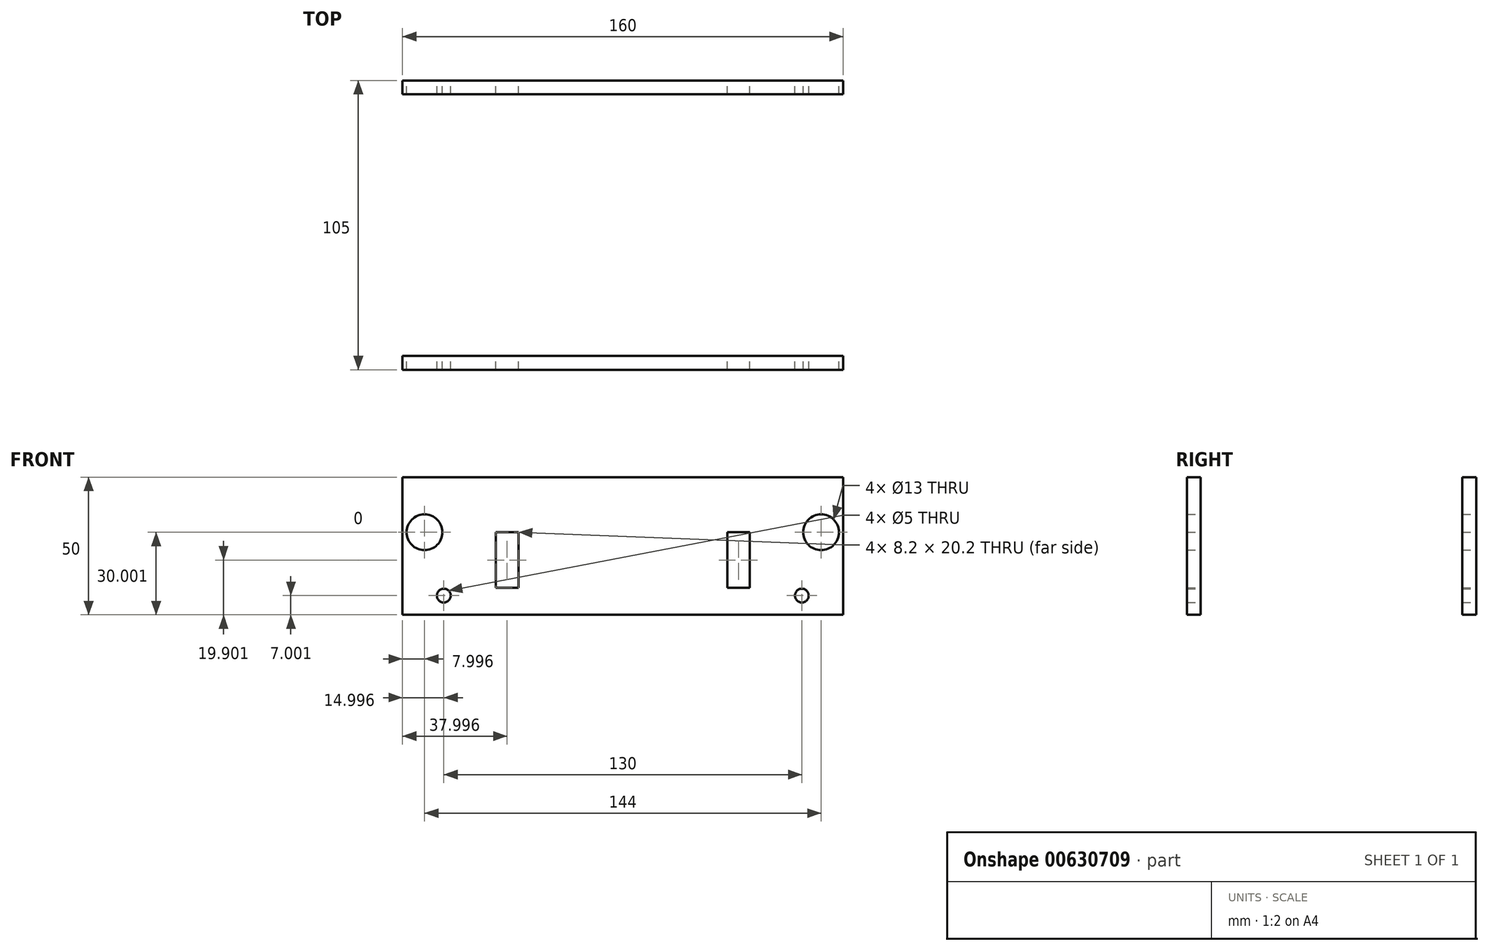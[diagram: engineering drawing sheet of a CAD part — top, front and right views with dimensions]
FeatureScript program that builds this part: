
annotation { "Feature Type Name" : "Feature", "Feature Type Description" : "" }
export const myFeature = defineFeature(function(context is Context, id is Id, definition is map)
    precondition{}
    {
        {
            var Q0;
            Q0=qCreatedBy(makeId("Front.planeOp"),FACE);
            var sketch = newSketch(context, id + "F0", { "sketchPlane" : qUnion([Q0])});
            skLineSegment(sketch, "E0.bottom", {"start": v(-54.53, 15.8) * mm, "end": v(105.47, 15.8) * mm});
            skLineSegment(sketch, "E0.top", {"start": v(-54.53, -34.2) * mm, "end": v(105.47, -34.2) * mm});
            skLineSegment(sketch, "E0.left", {"start": v(-54.53, 15.8) * mm, "end": v(-54.53, -34.2) * mm});
            skLineSegment(sketch, "E0.right", {"start": v(105.47, 15.8) * mm, "end": v(105.47, -34.2) * mm});
            skCircle(sketch, "E1", {"center": v(97.47, -4.2) * mm, "radius": 6.5 * mm});
            skLineSegment(sketch, "E2", {"start": v(25.47, 15.8) * mm, "end": v(25.47, -35.8) * mm, "construction": true});
            skPoint(sketch, "E2.endSnap0", {"position": v(25.47, -34.2) * mm});
            skLineSegment(sketch, "E3.bottom", {"start": v(63.37, -4.2) * mm, "end": v(71.57, -4.2) * mm});
            skLineSegment(sketch, "E3.top", {"start": v(63.37, -24.4) * mm, "end": v(71.57, -24.4) * mm});
            skLineSegment(sketch, "E3.left", {"start": v(63.37, -4.2) * mm, "end": v(63.37, -24.4) * mm});
            skLineSegment(sketch, "E3.right", {"start": v(71.57, -4.2) * mm, "end": v(71.57, -24.4) * mm});
            skLineSegment(sketch, "E4.MirrorCS", {"start": v(-12.43, -4.2) * mm, "end": v(-12.43, -24.4) * mm});
            skLineSegment(sketch, "E5.MirrorCS", {"start": v(-20.63, -4.2) * mm, "end": v(-20.63, -24.4) * mm});
            skLineSegment(sketch, "E6.MirrorCS", {"start": v(-12.43, -4.2) * mm, "end": v(-20.63, -4.2) * mm});
            skLineSegment(sketch, "E7.MirrorCS", {"start": v(-12.43, -24.4) * mm, "end": v(-20.63, -24.4) * mm});
            skCircle(sketch, "E8.MirrorC", {"center": v(-46.53, -4.2) * mm, "radius": 6.5 * mm});
            skPoint(sketch, "E9", {"position": v(67.47, -24.4) * mm});
            skPoint(sketch, "E10", {"position": v(-16.53, -24.4) * mm});
            skCircle(sketch, "E11", {"center": v(90.47, -27.2) * mm, "radius": 2.5 * mm});
            skCircle(sketch, "E12.MirrorC", {"center": v(-39.53, -27.2) * mm, "radius": 2.5 * mm});
            skSolve(sketch);
        }
        {
            var Q0;
            Q0 = qSketchRegion(id + "F0", true);
            extrude(context, id + "F1", {"entities" : qUnion([Q0]), "depth" : 5 * mm, "offsetDistance" : 25 * mm});
        }
        {
            var Q0;
            Q0=makeQuery(id+"F1.opExtrude","SWEPT_BODY",BODY,{"disambiguationData":[OSD([sQuery(id+"F0.wireOp",EDGE,"E0.bottom"),sQuery(id+"F0.wireOp",EDGE,"E0.top"),sQuery(id+"F0.wireOp",EDGE,"E0.left"),sQuery(id+"F0.wireOp",EDGE,"E0.right"),sQuery(id+"F0.wireOp",EDGE,"E1"),sQuery(id+"F0.wireOp",EDGE,"QShWiYwr-2bT6-ZryE-rk6D-aJS2m8MRligL"),sQuery(id+"F0.wireOp",EDGE,"d1fae640-989b-4966-b3a4-efb05116fdd30.MirrorC"),sQuery(id+"F0.wireOp",EDGE,"fb1e3ab4-b454-426e-8810-0b7114d907bb0.MirrorC")])]});
            transform(context, id + "F2", {"entities" : qUnion([Q0]), "transformType" : TransformType.TRANSLATION_3D, "dx" : 0 * mm, "dy" : 100 * mm, "dz" : 0 * mm, "makeCopy" : true});
        }
    });
